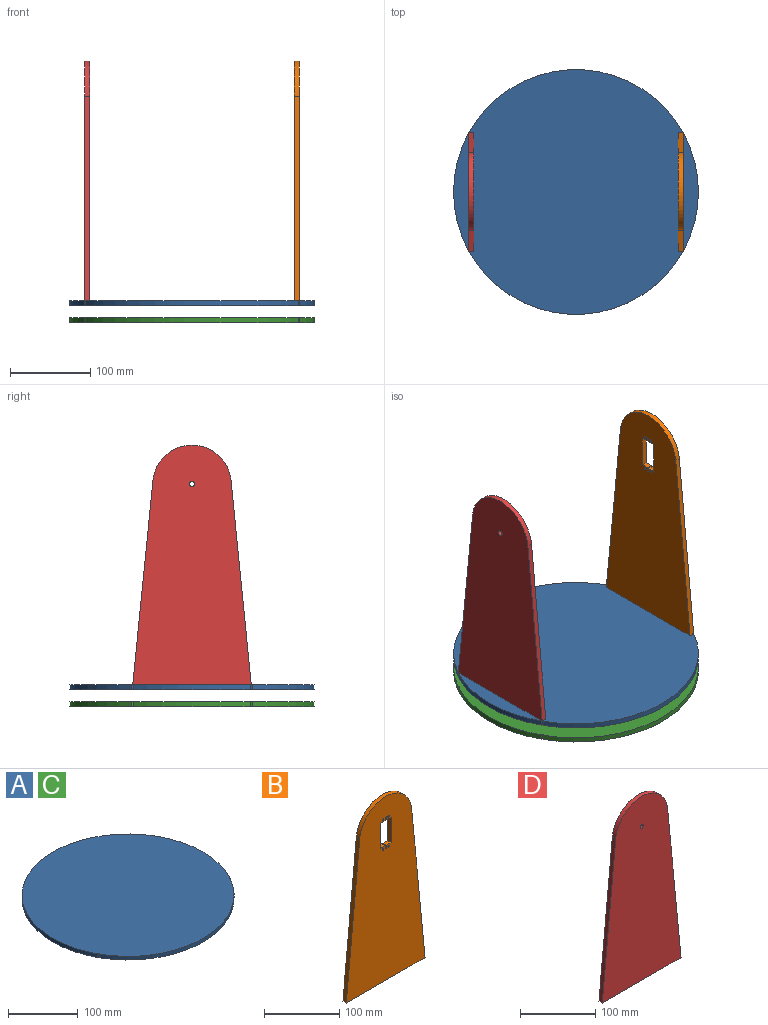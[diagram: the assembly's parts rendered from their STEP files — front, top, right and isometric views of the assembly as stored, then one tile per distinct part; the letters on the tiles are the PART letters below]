
ASSEMBLY  parts=4 mates=3
PART A: 10 faces, bbox 304.8x304.8x6.4 mm
  f0: cylinder r=152.4mm len=265.48mm, axis (0,0,-1), area 2046.3mm2, adj f4,f5,f6,f9
  f1: cylinder r=152.4mm len=145.37mm, axis (0,0,-1), area 962.2mm2, adj f4,f5,f8,f9
  f2: cylinder r=152.4mm len=265.48mm, axis (0,0,-1), area 2046.3mm2, adj f4,f5,f7,f8
  f3: cylinder r=152.4mm len=145.37mm, axis (0,0,-1), area 962.2mm2, adj f4,f5,f6,f7
  f4: plane 304.8x304.8mm, normal (0,0,1), area 72956.1mm2, adj f0,f1,f2,f3,f6,f7,f8,f9
  f5: plane 304.8x304.8mm, normal (0,0,-1), area 72956.1mm2, adj f0,f1,f2,f3,f6,f7,f8,f9
  f6: cylinder r=1.25mm len=6.35mm, axis (0,0,-1), area 24.9mm2, adj f0,f3,f4,f5
  f7: cylinder r=1.25mm len=6.35mm, axis (0,0,-1), area 24.9mm2, adj f2,f3,f4,f5
  f8: cylinder r=1.25mm len=6.35mm, axis (0,0,-1), area 24.9mm2, adj f1,f2,f4,f5
  f9: cylinder r=1.25mm len=6.35mm, axis (0,0,-1), area 24.9mm2, adj f0,f1,f4,f5
PART B: 22 faces, bbox 147.6x6.4x298.4 mm
  f0: plane 254.34x25.19mm, normal (-1,0,0.1), area 1622.9mm2, adj f1,f3,f4,f5
  f1: plane 147.56x6.35mm, normal (0,0,-1), area 937mm2, adj f0,f2,f4,f5
  f2: plane 254.34x25.19mm, normal (1,0,0.1), area 1622.9mm2, adj f1,f3,f4,f5
  f3: cylinder r=48.83mm len=97.19mm, axis (0,1,0), area 913mm2, adj f0,f2,f4,f5
  f4: plane 298.36x147.56mm, normal (0,-1,0), area 33533.6mm2, adj f0,f1,f2,f3,f6,f7,f8,f9
  f5: plane 298.36x147.56mm, normal (0,1,0), area 33533.6mm2, adj f0,f1,f2,f3,f6,f7,f8,f9
  f6: plane 9.1x6.35mm, normal (0,0,1), area 57.8mm2, adj f4,f5,f7,f17
  f7: plane 6.35x5mm, normal (1,0,0), area 31.8mm2, adj f4,f5,f6,f8
  f8: plane 6.35x2mm, normal (0,0,1), area 12.7mm2, adj f4,f5,f7,f9
  f9: plane 6.35x5mm, normal (-1,0,0), area 31.8mm2, adj f4,f5,f8,f10
  f10: plane 9.1x6.35mm, normal (0,0,1), area 57.8mm2, adj f4,f5,f9,f11
  f11: plane 41x6.35mm, normal (-1,0,0), area 260.3mm2, adj f4,f5,f10,f12
  f12: plane 9.1x6.35mm, normal (0,0,-1), area 57.8mm2, adj f4,f5,f11,f13
  f13: plane 6.35x5mm, normal (-1,0,0), area 31.8mm2, adj f4,f5,f12,f14
  f14: plane 6.35x2mm, normal (0,0,-1), area 12.7mm2, adj f4,f5,f13,f15
  f15: plane 6.35x5mm, normal (1,0,0), area 31.8mm2, adj f4,f5,f14,f16
  f16: plane 9.1x6.35mm, normal (0,0,-1), area 57.8mm2, adj f4,f5,f15,f17
  f17: plane 41x6.35mm, normal (1,0,0), area 260.3mm2, adj f4,f5,f6,f16
  f18: cylinder r=1.25mm len=6.35mm, axis (0,-1,0), area 49.9mm2, adj f4,f5
  f19: cylinder r=1.25mm len=6.35mm, axis (0,-1,0), area 49.9mm2, adj f4,f5
  f20: cylinder r=1.25mm len=6.35mm, axis (0,-1,0), area 49.9mm2, adj f4,f5
  f21: cylinder r=1.25mm len=6.35mm, axis (0,-1,0), area 49.9mm2, adj f4,f5
PART C: same geometry as A
PART D: 7 faces, bbox 147.6x6.4x298.4 mm
  f0: plane 254.34x25.19mm, normal (-1,0,0.1), area 1622.9mm2, adj f1,f3,f5,f6
  f1: plane 147.56x6.35mm, normal (0,0,-1), area 937mm2, adj f0,f2,f5,f6
  f2: plane 254.34x25.19mm, normal (1,0,0.1), area 1622.9mm2, adj f1,f3,f5,f6
  f3: cylinder r=48.83mm len=97.19mm, axis (0,1,0), area 913mm2, adj f0,f2,f5,f6
  f4: cylinder r=3.17mm len=6.35mm, axis (0,1,0), area 126.7mm2, adj f5,f6
  f5: plane 298.36x147.56mm, normal (0,-1,0), area 34369.7mm2, adj f0,f1,f2,f3,f4
  f6: plane 298.36x147.56mm, normal (0,1,0), area 34369.7mm2, adj f0,f1,f2,f3,f4
PLACE A t=(3.31,244.5,8.56)mm
PLACE B rot(axis=(0,0,1),90deg) t=(130.31,244.5,14.91)mm
PLACE C t=(3.31,244.5,-12.79)mm
PLACE D rot(axis=(0,0,1),90deg) t=(-130.04,244.5,14.91)mm
MATE fastened B.f1 <-> A.f8  axis (0,0,-1) through (136.66,318.28,14.91)mm
MATE revolute A.f0 <-> C.f0  axis (0,0,-1) through (3.31,244.5,8.56)mm
MATE fastened D.f1 <-> A.f7  axis (0,0,-1) through (-130.04,318.28,14.91)mm
